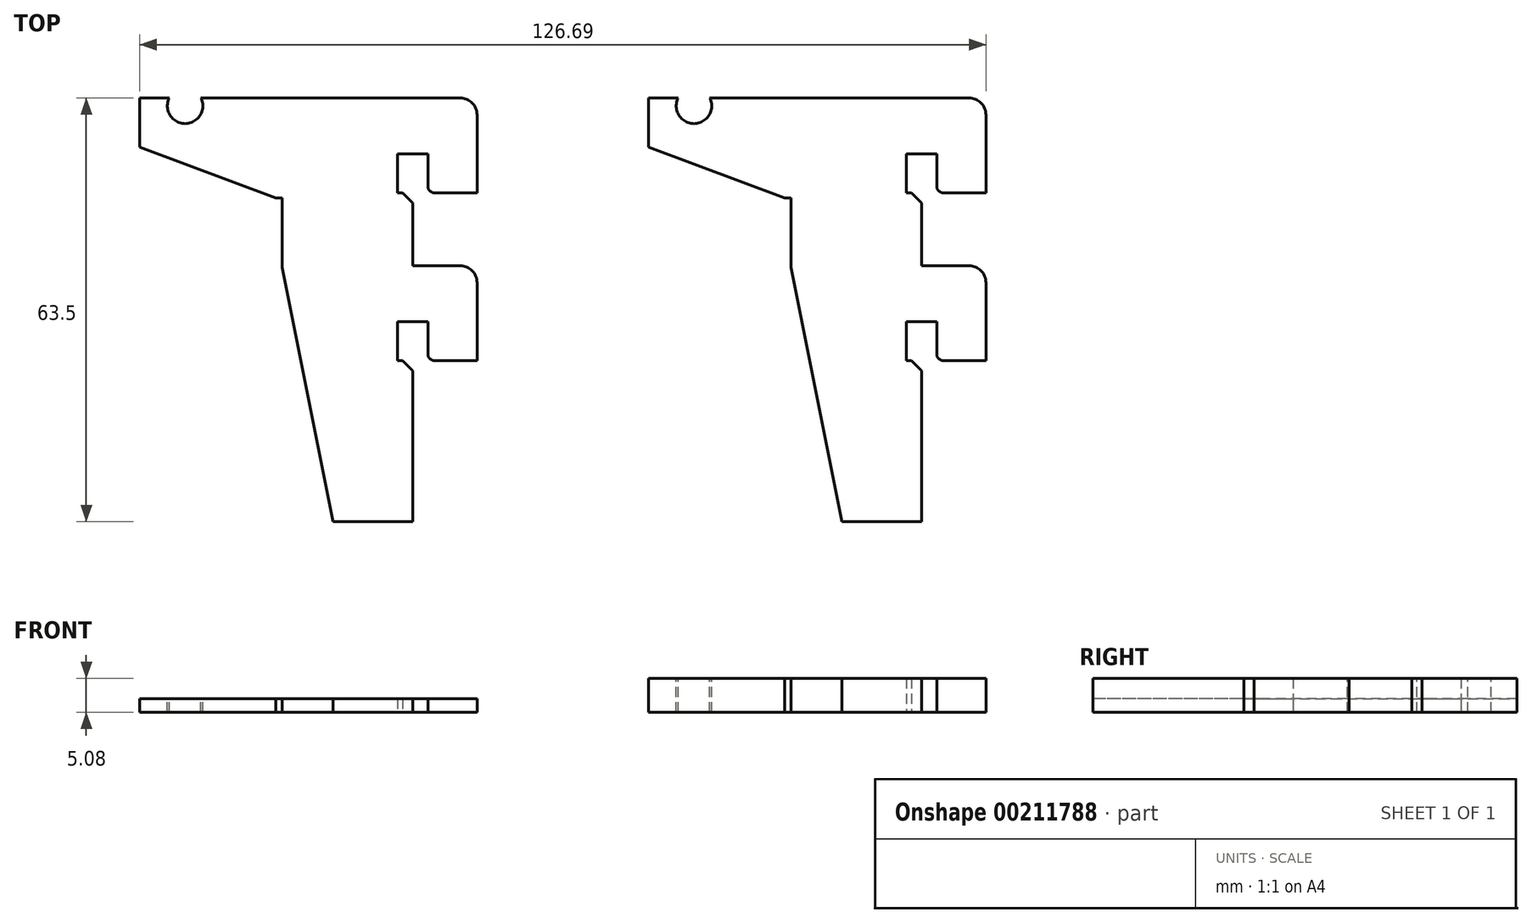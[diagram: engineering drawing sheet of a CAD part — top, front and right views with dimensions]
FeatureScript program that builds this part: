
annotation { "Feature Type Name" : "Feature", "Feature Type Description" : "" }
export const myFeature = defineFeature(function(context is Context, id is Id, definition is map)
    precondition{}
    {
        {
            var Q0;
            Q0=qCreatedBy(makeId("Top.planeOp"),FACE);
            var sketch = newSketch(context, id + "F0", { "sketchPlane" : qUnion([Q0])});
            skLineSegment(sketch, "E0.bottom", {"start": v(0, 0) * mm, "end": v(19.56, 0) * mm});
            skLineSegment(sketch, "E0.top", {"start": v(0, 63.5) * mm, "end": v(29.2, 63.5) * mm});
            skLineSegment(sketch, "E0.left", {"start": v(0, 0) * mm, "end": v(0, 63.5) * mm});
            skLineSegment(sketch, "E0.right", {"start": v(29.2, 24.13) * mm, "end": v(29.2, 38.35) * mm});
            skLineSegment(sketch, "E1.bottom", {"start": v(29.2, 49.28) * mm, "end": v(21.84, 49.28) * mm});
            skLineSegment(sketch, "E1.top", {"start": v(29.2, 38.35) * mm, "end": v(19.56, 38.35) * mm});
            skLineSegment(sketch, "E1.right", {"start": v(19.56, 49.28) * mm, "end": v(19.56, 38.35) * mm});
            skLineSegment(sketch, "E2.bottom", {"start": v(29.2, 24.13) * mm, "end": v(21.84, 24.13) * mm});
            skLineSegment(sketch, "E2.right", {"start": v(19.56, 24.13) * mm, "end": v(19.56, 0) * mm});
            skLineSegment(sketch, "E3.trimOffspring", {"start": v(29.2, 49.28) * mm, "end": v(29.2, 63.5) * mm});
            skLineSegment(sketch, "E4.bottom", {"start": v(19.56, 49.28) * mm, "end": v(17.27, 49.28) * mm});
            skLineSegment(sketch, "E4.top", {"start": v(21.84, 55.12) * mm, "end": v(17.27, 55.12) * mm});
            skLineSegment(sketch, "E4.left", {"start": v(21.84, 49.28) * mm, "end": v(21.84, 55.12) * mm});
            skLineSegment(sketch, "E4.right", {"start": v(17.27, 49.28) * mm, "end": v(17.27, 55.12) * mm});
            skLineSegment(sketch, "E5", {"start": v(19.56, 55.12) * mm, "end": v(19.56, 49.28) * mm, "construction": true});
            skLineSegment(sketch, "E6.bottom", {"start": v(19.56, 24.13) * mm, "end": v(17.27, 24.13) * mm});
            skLineSegment(sketch, "E6.top", {"start": v(21.84, 29.97) * mm, "end": v(17.27, 29.97) * mm});
            skLineSegment(sketch, "E6.left", {"start": v(21.84, 24.13) * mm, "end": v(21.84, 29.97) * mm});
            skLineSegment(sketch, "E6.right", {"start": v(17.27, 24.13) * mm, "end": v(17.27, 29.97) * mm});
            skLineSegment(sketch, "E7", {"start": v(19.56, 29.97) * mm, "end": v(19.56, 24.13) * mm, "construction": true});
            skSolve(sketch);
        }
        {
            var Q0;
            Q0=makeQuery(id+"F0.imprint","IMPRINT",FACE,{"disambiguationData":[TD([[makeQuery(id+"F0.imprint","IMPRINT",EDGE,{"derivedFrom":sQuery(id+"F0.wireOp",EDGE,"E0.bottom")}),1.0]])]});
            extrude(context, id + "F1", {"entities" : qUnion([Q0]), "depth" : 2.03 * mm});
        }
        {
            var Q0;
            Q0=makeQuery(id+"F1.opExtrude","SWEPT_EDGE",EDGE,{"disambiguationData":[OSD([sQuery(id+"F0.wireOp",EDGE,"E1.bottom"),sQuery(id+"F0.wireOp",EDGE,"E4.left")])]});
            var Q1;
            Q1=makeQuery(id+"F1.opExtrude","SWEPT_EDGE",EDGE,{"disambiguationData":[OSD([sQuery(id+"F0.wireOp",EDGE,"E2.bottom"),sQuery(id+"F0.wireOp",EDGE,"E6.left")])]});
            fillet(context, id + "F2", {"entities" : qUnion([Q0, Q1]), "radius" : 1.02 * mm, "tangentPropagation" : true, "allowEdgeOverflow" : false});
        }
        {
            var Q0;
            Q0=makeQuery(id+"F1.opExtrude","SWEPT_EDGE",EDGE,{"disambiguationData":[OSD([sQuery(id+"F0.wireOp",EDGE,"E1.right"),sQuery(id+"F0.wireOp",EDGE,"E4.bottom")])]});
            var Q1;
            Q1=makeQuery(id+"F1.opExtrude","SWEPT_EDGE",EDGE,{"disambiguationData":[OSD([sQuery(id+"F0.wireOp",EDGE,"E2.right"),sQuery(id+"F0.wireOp",EDGE,"E6.bottom")])]});
            chamfer(context, id + "F3", {"entities" : qUnion([Q0, Q1]), "width" : 1.52 * mm, "tangentPropagation" : true});
        }
        {
            var Q0;
            Q0=makeQuery(id+"F1.opExtrude","SWEPT_EDGE",EDGE,{"disambiguationData":[OSD([sQuery(id+"F0.wireOp",EDGE,"E0.right"),sQuery(id+"F0.wireOp",EDGE,"E1.top")])]});
            var Q1;
            Q1=makeQuery(id+"F1.opExtrude","SWEPT_EDGE",EDGE,{"disambiguationData":[OSD([sQuery(id+"F0.wireOp",EDGE,"E0.top"),sQuery(id+"F0.wireOp",EDGE,"E3.trimOffspring")])]});
            fillet(context, id + "F4", {"entities" : qUnion([Q0, Q1]), "radius" : 2.54 * mm, "tangentPropagation" : true, "allowEdgeOverflow" : false});
        }
        {
            var Q0;
            Q0=makeQuery(id+"F1.opExtrude","CAP_FACE",FACE,{"disambiguationData":[OSD([sQuery(id+"F0.wireOp",EDGE,"E0.bottom"),sQuery(id+"F0.wireOp",EDGE,"E0.top"),sQuery(id+"F0.wireOp",EDGE,"E0.left"),sQuery(id+"F0.wireOp",EDGE,"E0.right"),sQuery(id+"F0.wireOp",EDGE,"E1.bottom"),sQuery(id+"F0.wireOp",EDGE,"E1.top"),sQuery(id+"F0.wireOp",EDGE,"E1.right"),sQuery(id+"F0.wireOp",EDGE,"E2.bottom"),sQuery(id+"F0.wireOp",EDGE,"E2.right"),sQuery(id+"F0.wireOp",EDGE,"E3.trimOffspring"),sQuery(id+"F0.wireOp",EDGE,"E4.bottom"),sQuery(id+"F0.wireOp",EDGE,"E4.top"),sQuery(id+"F0.wireOp",EDGE,"E4.left"),sQuery(id+"F0.wireOp",EDGE,"E4.right"),sQuery(id+"F0.wireOp",EDGE,"E6.bottom"),sQuery(id+"F0.wireOp",EDGE,"E6.top"),sQuery(id+"F0.wireOp",EDGE,"E6.left"),sQuery(id+"F0.wireOp",EDGE,"E6.right")])],"isStart":false});
            var sketch = newSketch(context, id + "F5", { "sketchPlane" : qUnion([Q0])});
            skPoint(sketch, "E8.oppositeSnap0", {"position": v(18.8, 48.51) * mm});
            skLineSegment(sketch, "E8.bottom", {"start": v(0, 63.5) * mm, "end": v(-21.28, 63.5) * mm});
            skLineSegment(sketch, "E8.top", {"start": v(0, 48.51) * mm, "end": v(-21.28, 48.51) * mm});
            skLineSegment(sketch, "E8.left", {"start": v(0, 63.5) * mm, "end": v(0, 48.51) * mm});
            skLineSegment(sketch, "E8.right", {"start": v(-21.28, 63.5) * mm, "end": v(-21.28, 48.51) * mm});
            skCircle(sketch, "E9", {"center": v(-14.5, 62.3) * mm, "radius": 2.65 * mm});
            skSolve(sketch);
        }
        {
            var Q0;
            Q0=makeQuery(id+"F5.imprint","IMPRINT",FACE,{"disambiguationData":[TD([[makeQuery(id+"F5.imprint","IMPRINT",EDGE,{"derivedFrom":sQuery(id+"F5.wireOp",EDGE,"E8.top")}),-1.0]])]});
            extrude(context, id + "F6", {"entities" : qUnion([Q0]), "operationType" : NewBodyOperationType.ADD, "oppositeDirection" : true, "depth" : 2.03 * mm});
        }
        {
            var Q0;
            Q0=makeQuery(id+"F6.opExtrude","SWEPT_EDGE",EDGE,{"disambiguationData":[OSD([sQuery(id+"F5.wireOp",EDGE,"E8.top"),sQuery(id+"F5.wireOp",EDGE,"E8.right")])]});
            chamfer(context, id + "F7", {"entities" : qUnion([Q0]), "chamferType" : ChamferType.TWO_OFFSETS, "width1" : 7.62 * mm, "oppositeDirection" : false, "width2" : 20.32 * mm, "tangentPropagation" : true});
        }
        {
            var Q0;
            Q0=makeQuery(id+"F1.opExtrude","SWEPT_EDGE",EDGE,{"disambiguationData":[OSD([sQuery(id+"F0.wireOp",EDGE,"E0.bottom"),sQuery(id+"F0.wireOp",EDGE,"E0.left")])]});
            chamfer(context, id + "F8", {"entities" : qUnion([Q0]), "chamferType" : ChamferType.TWO_OFFSETS, "width1" : 7.62 * mm, "oppositeDirection" : false, "width2" : 38.1 * mm, "tangentPropagation" : true});
        }
        {
            var Q0;
            Q0=makeQuery(id+"F1.opExtrude","SWEPT_BODY",BODY,{"disambiguationData":[OSD([sQuery(id+"F0.wireOp",EDGE,"E0.bottom"),sQuery(id+"F0.wireOp",EDGE,"E0.top"),sQuery(id+"F0.wireOp",EDGE,"E0.left"),sQuery(id+"F0.wireOp",EDGE,"E0.right"),sQuery(id+"F0.wireOp",EDGE,"E1.bottom"),sQuery(id+"F0.wireOp",EDGE,"E1.top"),sQuery(id+"F0.wireOp",EDGE,"E1.right"),sQuery(id+"F0.wireOp",EDGE,"E2.bottom"),sQuery(id+"F0.wireOp",EDGE,"E2.right"),sQuery(id+"F0.wireOp",EDGE,"E3.trimOffspring"),sQuery(id+"F0.wireOp",EDGE,"E4.bottom"),sQuery(id+"F0.wireOp",EDGE,"E4.top"),sQuery(id+"F0.wireOp",EDGE,"E4.left"),sQuery(id+"F0.wireOp",EDGE,"E4.right"),sQuery(id+"F0.wireOp",EDGE,"E6.bottom"),sQuery(id+"F0.wireOp",EDGE,"E6.top"),sQuery(id+"F0.wireOp",EDGE,"E6.left"),sQuery(id+"F0.wireOp",EDGE,"E6.right")])]});
            transform(context, id + "F9", {"entities" : qUnion([Q0]), "transformType" : TransformType.TRANSLATION_3D, "dx" : 76.2 * mm, "dy" : 0 * mm, "dz" : 0 * mm, "makeCopy" : true});
        }
        {
            var Q0;
            Q0=makeQuery(id+"F9.opPattern","COPY",FACE,{"derivedFrom":makeQuery(id+"F6.boolean.opBoolean","MERGE",FACE,{"derivedFrom":[makeQuery(id+"F1.opExtrude","CAP_FACE",FACE,{"disambiguationData":[OSD([sQuery(id+"F0.wireOp",EDGE,"E0.bottom"),sQuery(id+"F0.wireOp",EDGE,"E0.top"),sQuery(id+"F0.wireOp",EDGE,"E0.left"),sQuery(id+"F0.wireOp",EDGE,"E0.right"),sQuery(id+"F0.wireOp",EDGE,"E1.bottom"),sQuery(id+"F0.wireOp",EDGE,"E1.top"),sQuery(id+"F0.wireOp",EDGE,"E1.right"),sQuery(id+"F0.wireOp",EDGE,"E2.bottom"),sQuery(id+"F0.wireOp",EDGE,"E2.right"),sQuery(id+"F0.wireOp",EDGE,"E3.trimOffspring"),sQuery(id+"F0.wireOp",EDGE,"E4.bottom"),sQuery(id+"F0.wireOp",EDGE,"E4.top"),sQuery(id+"F0.wireOp",EDGE,"E4.left"),sQuery(id+"F0.wireOp",EDGE,"E4.right"),sQuery(id+"F0.wireOp",EDGE,"E6.bottom"),sQuery(id+"F0.wireOp",EDGE,"E6.top"),sQuery(id+"F0.wireOp",EDGE,"E6.left"),sQuery(id+"F0.wireOp",EDGE,"E6.right")])],"isStart":true}),makeQuery(id+"F6.opExtrude","CAP_FACE",FACE,{"disambiguationData":[OSD([sQuery(id+"F5.wireOp",EDGE,"E8.bottom"),sQuery(id+"F5.wireOp",EDGE,"E8.top"),sQuery(id+"F5.wireOp",EDGE,"E8.left"),sQuery(id+"F5.wireOp",EDGE,"E8.right"),sQuery(id+"F5.wireOp",EDGE,"E9")])],"isStart":false})]}),"instanceName":"1"});
            extrude(context, id + "F10", {"entities" : qUnion([Q0]), "operationType" : NewBodyOperationType.ADD, "oppositeDirection" : true, "depth" : 5.08 * mm});
        }
    });
